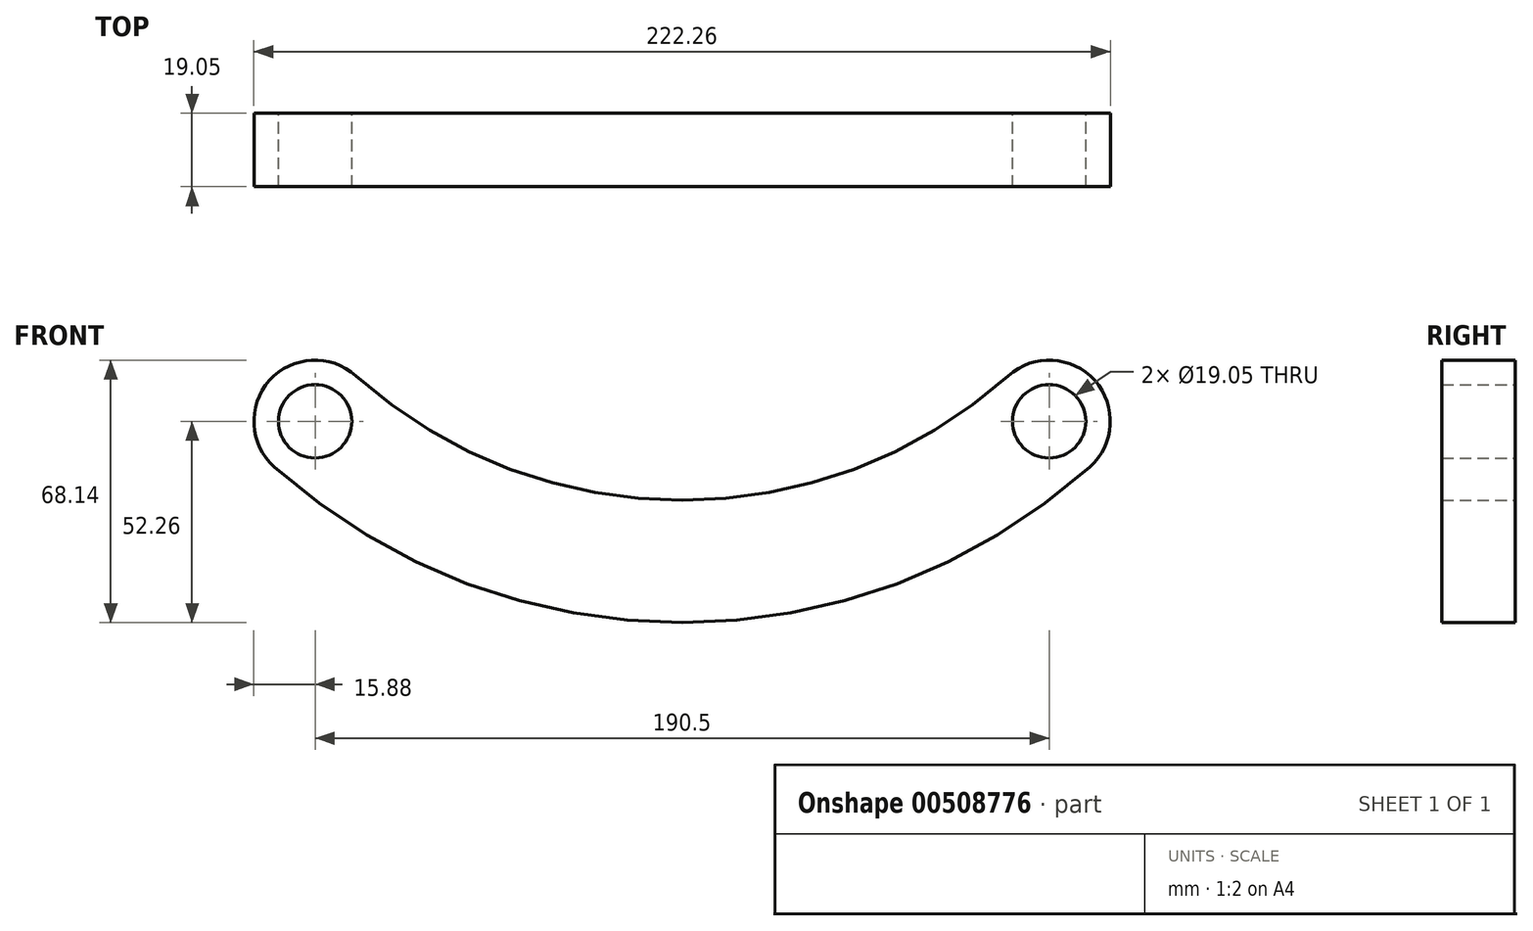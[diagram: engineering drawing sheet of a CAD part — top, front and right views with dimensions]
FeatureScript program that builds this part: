
annotation { "Feature Type Name" : "Feature", "Feature Type Description" : "" }
export const myFeature = defineFeature(function(context is Context, id is Id, definition is map)
    precondition{}
    {
        {
            var Q0;
            Q0=qCreatedBy(makeId("Front.planeOp"),FACE);
            var sketch = newSketch(context, id + "F0", { "sketchPlane" : qUnion([Q0])});
            skCircle(sketch, "E0", {"center": v(0, 0) * mm, "radius": 9.53 * mm});
            skCircle(sketch, "E1", {"center": v(190.5, 0) * mm, "radius": 9.53 * mm});
            skArc(sketch, "E2", {"start": v(10.58, 11.83) * mm, "mid": v(-11.83, 10.58) * mm, "end": v(-10.58, -11.83) * mm});
            skArc(sketch, "E3", {"start": v(201.08, -11.83) * mm, "mid": v(202.33, 10.58) * mm, "end": v(179.92, 11.83) * mm});
            skArc(sketch, "E4", {"start": v(10.58, 11.83) * mm, "mid": v(95.25, -20.5) * mm, "end": v(179.92, 11.83) * mm});
            skArc(sketch, "E5", {"start": v(-10.58, -11.83) * mm, "mid": v(95.25, -52.26) * mm, "end": v(201.08, -11.83) * mm});
            skSolve(sketch);
        }
        {
            var Q0;
            {var subQ0=sQuery(id+"F0.wireOp",EDGE,"E4");Q0=makeQuery(id+"F0.imprint","IMPRINT",FACE,{"disambiguationData":[TD([[makeQuery(id+"F0.imprint","IMPRINT",EDGE,{"derivedFrom":subQ0}),-1.0]])]});}
            var Q1;
            Q1=makeQuery(id+"F0.imprint","IMPRINT",FACE,{"disambiguationData":[TD([[makeQuery(id+"F0.imprint","IMPRINT",EDGE,{"derivedFrom":sQuery(id+"F0.wireOp",EDGE,"E0")}),-1.0]])]});
            var Q2;
            Q2=makeQuery(id+"F0.imprint","IMPRINT",FACE,{"disambiguationData":[TD([[makeQuery(id+"F0.imprint","IMPRINT",EDGE,{"derivedFrom":sQuery(id+"F0.wireOp",EDGE,"E1")}),-1.0]])]});
            extrude(context, id + "F1", {"entities" : qUnion([Q0, Q1, Q2]), "depth" : 19.05 * mm});
        }
    });
